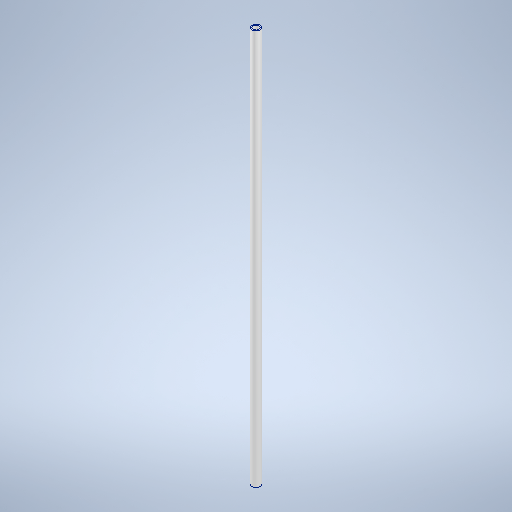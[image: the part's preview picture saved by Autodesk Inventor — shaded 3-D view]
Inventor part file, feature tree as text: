
AUTODESK INVENTOR PART (.ipt)
format: ipt  version: 2025 (Build 290162000, 162)  size: 252,928 bytes
history: native  units: mm
features: other x1, extrude x1, sketch x1
ambient origin geometry x8: Origin, YZ Plane, XZ Plane, XY Plane, X Axis, Y Axis, Z Axis, Center Point
bodies: Body1 (feature_tree)
feature tree (3):
  other  "Těleso1"
  extrude  "Vysunutí1"  Depth=8.0mm
  sketch  "Náčrt1"
